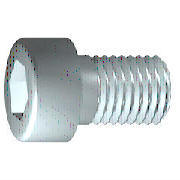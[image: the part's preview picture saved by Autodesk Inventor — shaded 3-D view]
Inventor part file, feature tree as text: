
AUTODESK INVENTOR PART (.ipt)
format: ipt  version: 2021 (Build 250183000, 183)  size: 184,832 bytes
history: native  units: mm (DEFAULTED — no unit token found)
features: sketch x2, extrude x1, plane x1, fillet x1
ambient origin geometry x7: Origin, YZ Plane, XY Plane, X Axis, Y Axis, Z Axis, Center Point
bodies: Solid1 (feature_tree), Body (feature_tree)
feature tree (5):
  extrude  "Slot"  Depth=6.0mm
  plane  "Work Plane1"
  fillet  "Fillet2"  Radius=6.0mm
  sketch  "Sketch1"  dims[d1=18.0mm d2=0.61355mm d3=6.0mm]
  sketch  "Sketch2"  dims[d4=3.0mm d5=60.0deg d6=6.0mm d7=6.0mm d8=5.773503mm d9=10.0mm d10=90.0deg d11=10.0mm d12=0.0mm d13=18.0mm d14=0.0mm d15=0.61345mm d16=0.61345mm d17=0.6mm d19=0.0mm d26=60.0mm d27=45.0deg d28=0.0mm d29=0.0mm d30=0.1mm]
